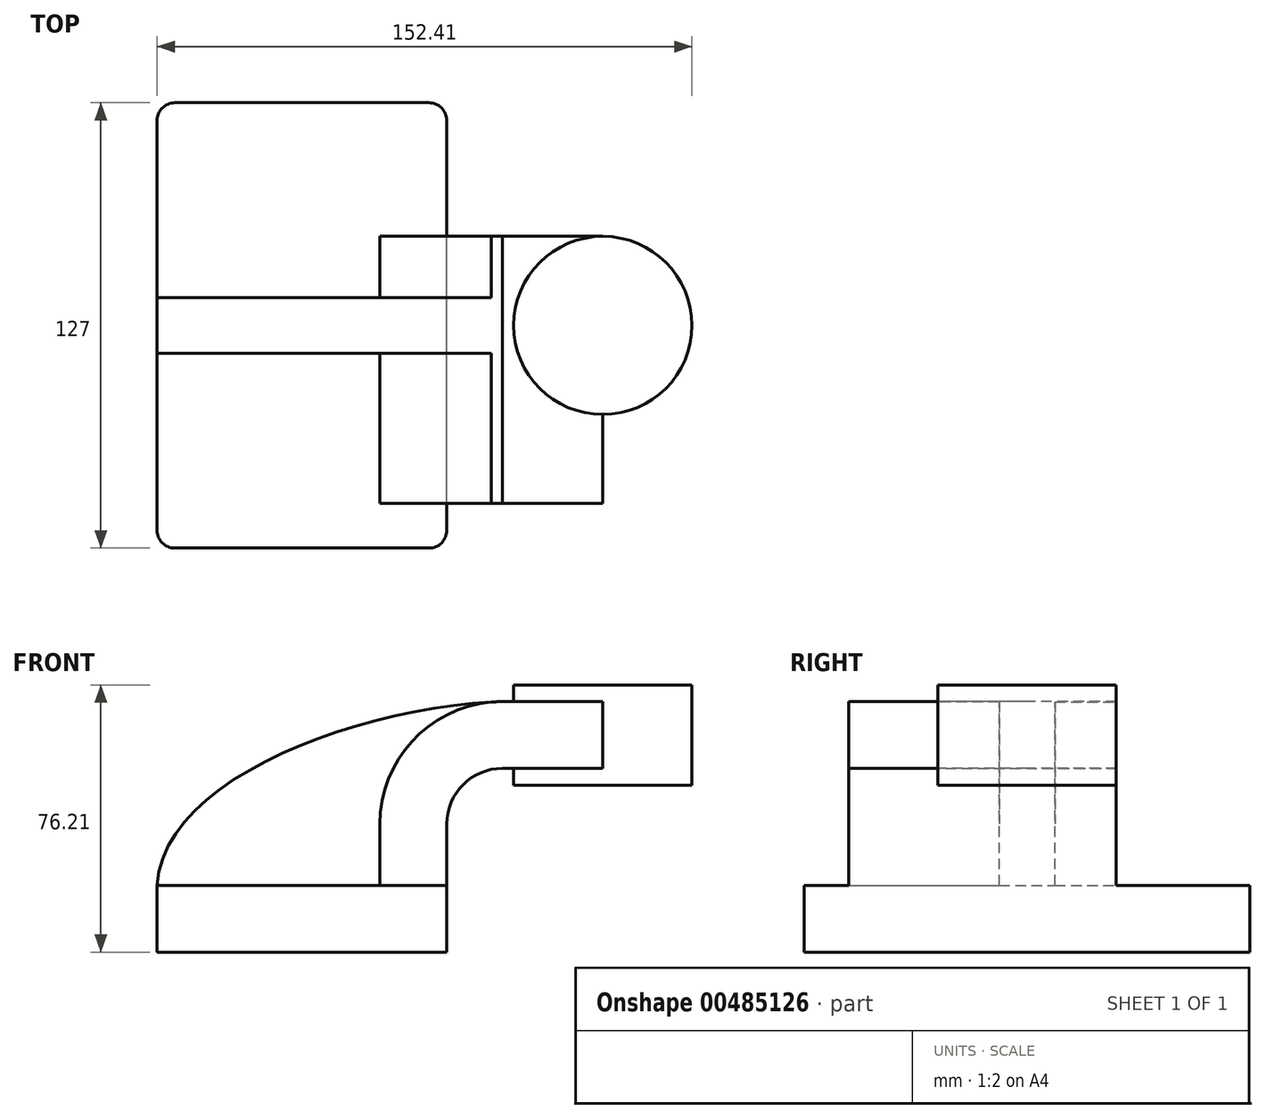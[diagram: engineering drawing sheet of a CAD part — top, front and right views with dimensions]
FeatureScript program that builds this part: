
annotation { "Feature Type Name" : "Feature", "Feature Type Description" : "" }
export const myFeature = defineFeature(function(context is Context, id is Id, definition is map)
    precondition{}
    {
        {
            var Q0;
            Q0=qCreatedBy(makeId("Front.planeOp"),FACE);
            var sketch = newSketch(context, id + "F0", { "sketchPlane" : qUnion([Q0])});
            skLineSegment(sketch, "E0.rect.bottom", {"start": v(-41.28, 9.52) * mm, "end": v(41.28, 9.52) * mm});
            skLineSegment(sketch, "E0.rect.top", {"start": v(-41.28, -9.52) * mm, "end": v(41.28, -9.52) * mm});
            skLineSegment(sketch, "E0.rect.left", {"start": v(-41.28, 9.52) * mm, "end": v(-41.28, -9.52) * mm});
            skLineSegment(sketch, "E0.rect.right", {"start": v(41.28, 9.52) * mm, "end": v(41.28, -9.52) * mm});
            skPoint(sketch, "E0.rect.middle", {"position": v(0, 0) * mm});
            skLineSegment(sketch, "E1", {"start": v(41.28, 9.52) * mm, "end": v(41.28, 27) * mm});
            skArc(sketch, "E2", {"start": v(41.28, 27) * mm, "mid": v(45.92, 38.23) * mm, "end": v(57.15, 42.88) * mm});
            skLineSegment(sketch, "E3", {"start": v(57.15, 42.88) * mm, "end": v(85.72, 42.88) * mm});
            skLineSegment(sketch, "E4.rect.bottom", {"start": v(60.32, 38.1) * mm, "end": v(111.12, 38.1) * mm});
            skLineSegment(sketch, "E4.rect.top", {"start": v(60.32, 66.68) * mm, "end": v(111.12, 66.68) * mm});
            skLineSegment(sketch, "E4.rect.left", {"start": v(60.32, 38.1) * mm, "end": v(60.32, 66.68) * mm});
            skLineSegment(sketch, "E4.rect.right", {"start": v(111.13, 38.1) * mm, "end": v(111.12, 66.68) * mm});
            skPoint(sketch, "E4.rect.middle", {"position": v(85.72, 52.39) * mm});
            skLineSegment(sketch, "E5.0", {"start": v(57.15, 61.93) * mm, "end": v(85.72, 61.93) * mm});
            skArc(sketch, "E5.1", {"start": v(22.23, 27) * mm, "mid": v(32.45, 51.7) * mm, "end": v(57.15, 61.93) * mm});
            skLineSegment(sketch, "E5.2", {"start": v(22.23, 9.52) * mm, "end": v(22.23, 27) * mm});
            skLineSegment(sketch, "E6", {"start": v(85.72, 38.1) * mm, "end": v(85.72, 66.68) * mm});
            skFitSpline(sketch, "E7", {"points": [v(-41.28, 9.53) * mm, v(57.15, 61.93) * mm], "startDerivative": vector(5.2, 92.34) * mm, "endDerivative": vector(120.92, 4.22) * mm});
            skSolve(sketch);
        }
        {
            var Q0;
            Q0=makeQuery(id+"F0.imprint","IMPRINT",FACE,{"disambiguationData":[TD([[makeQuery(id+"F0.imprint","IMPRINT",EDGE,{"derivedFrom":sQuery(id+"F0.wireOp",EDGE,"E0.rect.top")}),1.0]])]});
            extrude(context, id + "F1", {"entities" : qUnion([Q0]), "endBound" : BoundingType.SYMMETRIC, "depth" : 127 * mm});
        }
        {
            var Q0;
            {var subQ9=sQuery(id+"F0.wireOp",EDGE,"E1");Q0=makeQuery(id+"F0.imprint","IMPRINT",FACE,{"disambiguationData":[TD([[makeQuery(id+"F0.imprint","IMPRINT",EDGE,{"derivedFrom":subQ9}),1.0]])]});}
            var Q1;
            {var subQ0=sQuery(id+"F0.wireOp",EDGE,"E6");var subQ1=sQuery(id+"F0.wireOp",EDGE,"E3");var subQ2=makeQuery(id+"F0.imprint","INTERSECT",VERTEX,{"derivedFrom":[subQ1,subQ0]});Q1=makeQuery(id+"F0.imprint","IMPRINT",FACE,{"disambiguationData":[TD([[makeQuery(id+"F0.imprint","IMPRINT",EDGE,{"disambiguationData":[TD([[subQ2,1.0]])],"derivedFrom":subQ1}),1.0]])]});}
            extrude(context, id + "F2", {"entities" : qUnion([Q0, Q1]), "operationType" : NewBodyOperationType.ADD, "endBound" : BoundingType.SYMMETRIC, "depth" : 50.8 * mm});
        }
        {
            var Q0;
            {var subQ3=sQuery(id+"F0.wireOp",EDGE,"E5.2");Q0=makeQuery(id+"F0.imprint","IMPRINT",FACE,{"disambiguationData":[TD([[makeQuery(id+"F0.imprint","IMPRINT",EDGE,{"derivedFrom":subQ3}),1.0]])]});}
            extrude(context, id + "F3", {"entities" : qUnion([Q0]), "operationType" : NewBodyOperationType.ADD, "endBound" : BoundingType.SYMMETRIC, "depth" : 15.88 * mm});
        }
        {
            var Q0;
            {var subQ5=sQuery(id+"F0.wireOp",EDGE,"E4.rect.right");Q0=makeQuery(id+"F0.imprint","IMPRINT",FACE,{"disambiguationData":[TD([[makeQuery(id+"F0.imprint","IMPRINT",EDGE,{"derivedFrom":subQ5}),1.0]])]});}
            var Q1;
            Q1=sQuery(id+"F0.wireOp",EDGE,"E6");
            revolve(context, id + "F4", {"operationType" : NewBodyOperationType.ADD, "entities" : qUnion([Q0]), "axis" : qUnion([Q1]), "revolveType" : RevolveType.FULL});
        }
        {
            var Q0;
            Q0=makeQuery(id+"F1.opExtrude","CAP_EDGE",EDGE,{"disambiguationData":[OSD([sQuery(id+"F0.wireOp",EDGE,"E0.rect.right")])],"isStart":false});
            var Q1;
            Q1=makeQuery(id+"F1.opExtrude","CAP_EDGE",EDGE,{"disambiguationData":[OSD([sQuery(id+"F0.wireOp",EDGE,"E0.rect.left")])],"isStart":false});
            var Q2;
            Q2=makeQuery(id+"F1.opExtrude","CAP_EDGE",EDGE,{"disambiguationData":[OSD([sQuery(id+"F0.wireOp",EDGE,"E0.rect.right")])],"isStart":true});
            var Q3;
            Q3=makeQuery(id+"F1.opExtrude","CAP_EDGE",EDGE,{"disambiguationData":[OSD([sQuery(id+"F0.wireOp",EDGE,"E0.rect.left")])],"isStart":true});
            fillet(context, id + "F5", {"entities" : qUnion([Q0, Q1, Q2, Q3]), "radius" : 5.08 * mm, "tangentPropagation" : true, "allowEdgeOverflow" : false});
        }
        {
            var Q0;
            Q0=makeQuery(id+"F2.opExtrude","CAP_FACE",FACE,{"disambiguationData":[OSD([sQuery(id+"F0.wireOp",EDGE,"E0.rect.bottom"),sQuery(id+"F0.wireOp",EDGE,"E1"),sQuery(id+"F0.wireOp",EDGE,"E2"),sQuery(id+"F0.wireOp",EDGE,"E3"),sQuery(id+"F0.wireOp",EDGE,"E5.0"),sQuery(id+"F0.wireOp",EDGE,"E5.1"),sQuery(id+"F0.wireOp",EDGE,"E5.2"),sQuery(id+"F0.wireOp",EDGE,"E6"),sQuery(id+"F0.wireOp",EDGE,"E7")])],"isStart":false});
            extrude(context, id + "F6", {"entities" : qUnion([Q0]), "operationType" : NewBodyOperationType.ADD, "depth" : 25.4 * mm});
        }
    });
